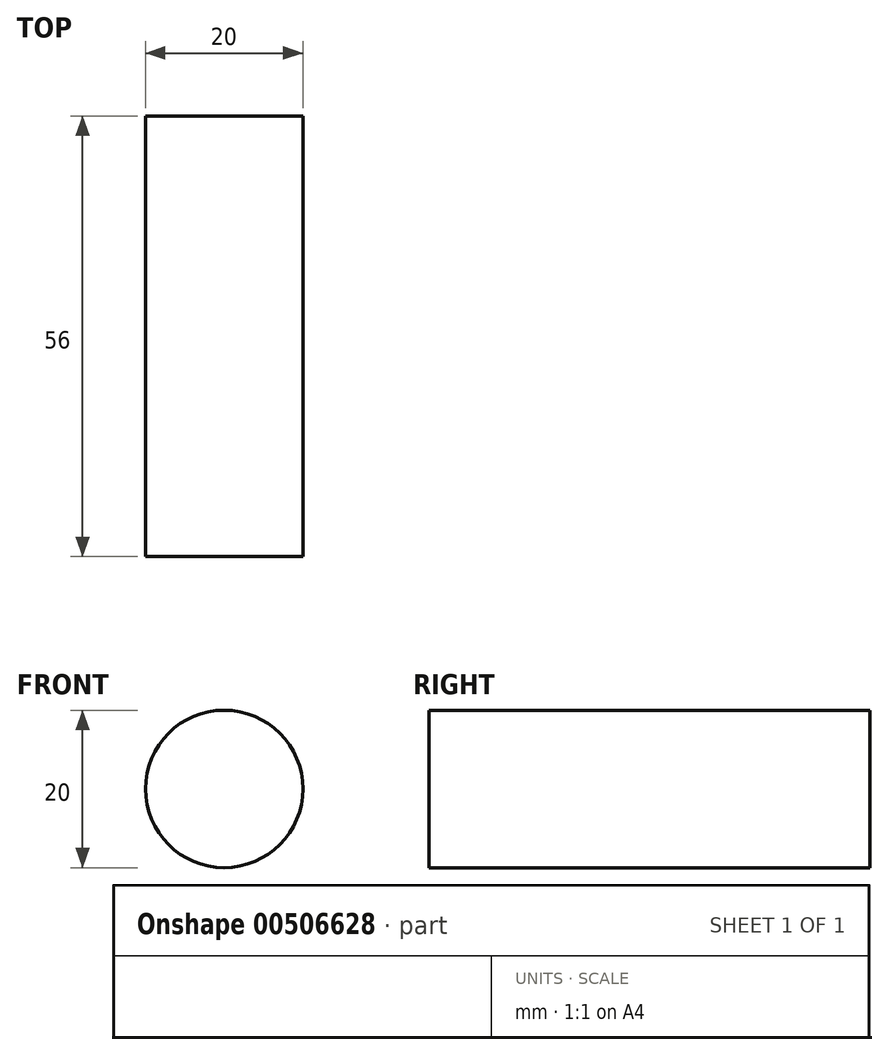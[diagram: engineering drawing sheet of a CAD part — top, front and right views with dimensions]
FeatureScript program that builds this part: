
annotation { "Feature Type Name" : "Feature", "Feature Type Description" : "" }
export const myFeature = defineFeature(function(context is Context, id is Id, definition is map)
    precondition{}
    {
        {
            var Q0;
            Q0=qCreatedBy(makeId("Front.planeOp"),FACE);
            var sketch = newSketch(context, id + "F0", { "sketchPlane" : qUnion([Q0])});
            skCircle(sketch, "E0", {"center": v(0, 0) * mm, "radius": 10 * mm});
            skSolve(sketch);
        }
        {
            var Q0;
            Q0=qSketchRegion(id+"F0",true);
            extrude(context, id + "F1", {"entities" : qUnion([Q0]), "depth" : 56 * mm, "symmetric" : true});
        }
    });
